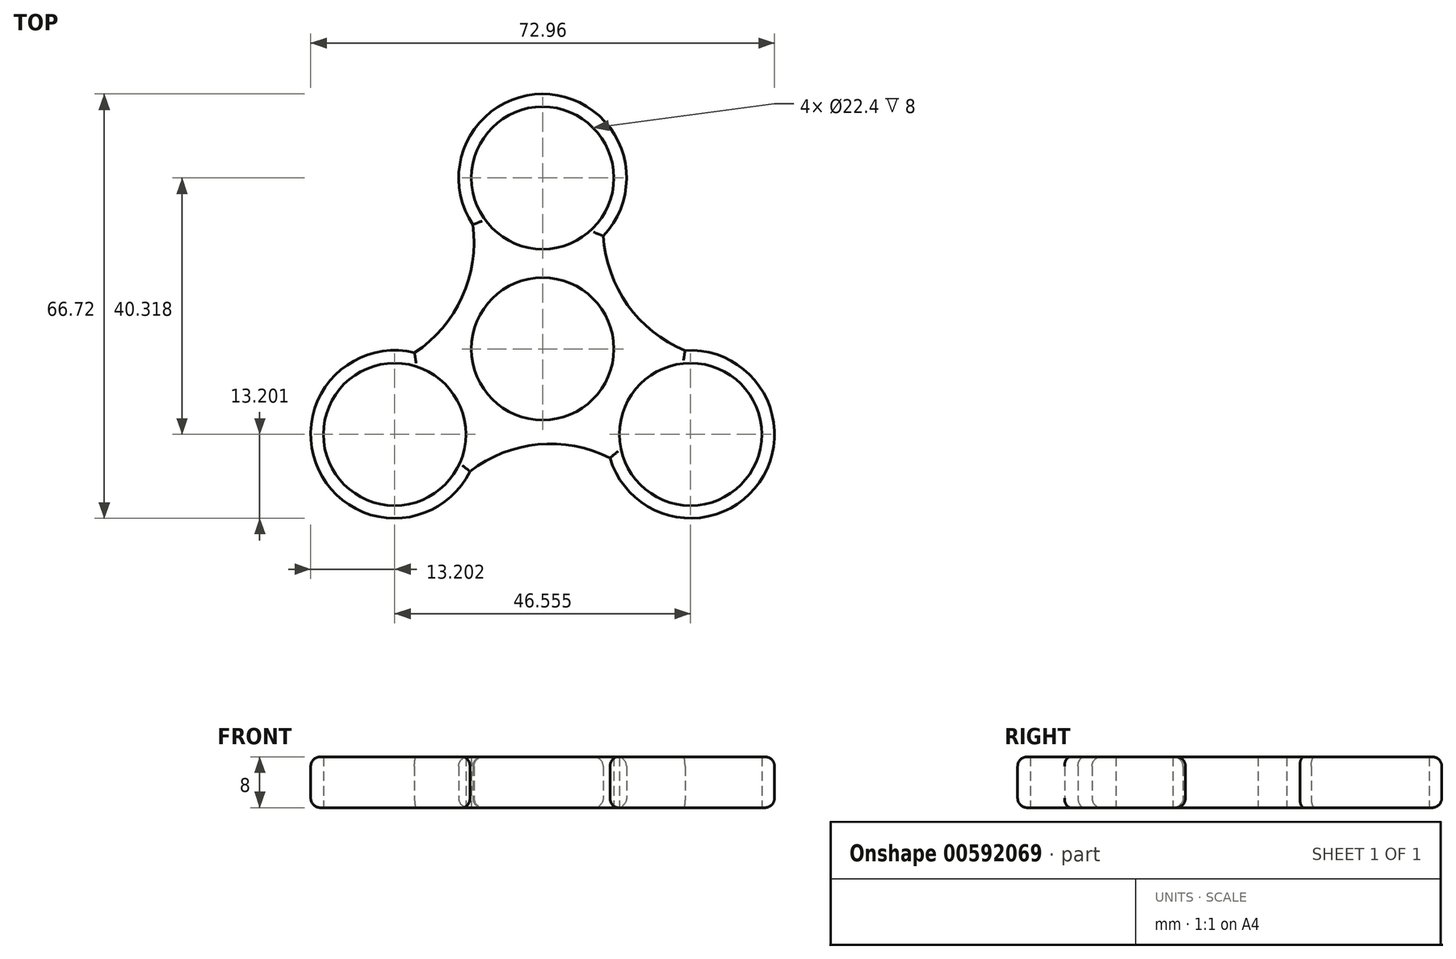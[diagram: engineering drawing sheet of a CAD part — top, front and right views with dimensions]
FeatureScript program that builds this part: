
annotation { "Feature Type Name" : "Feature", "Feature Type Description" : "" }
export const myFeature = defineFeature(function(context is Context, id is Id, definition is map)
    precondition{}
    {
        {
            var Q0;
            Q0=qCreatedBy(makeId("Top.planeOp"),FACE);
            var sketch = newSketch(context, id + "F0", { "sketchPlane" : qUnion([Q0])});
            skCircle(sketch, "E0", {"center": v(0, 0) * mm, "radius": 11.2 * mm});
            skCircle(sketch, "E1", {"center": v(0, 26.88) * mm, "radius": 11.2 * mm});
            skArc(sketch, "E2", {"start": v(9.54, 17.76) * mm, "mid": v(1.14, 40.03) * mm, "end": v(-10.97, 19.54) * mm});
            skArc(sketch, "E3.1.0", {"start": v(-20.15, -0.61) * mm, "mid": v(-35.24, -19.03) * mm, "end": v(-11.43, -19.27) * mm});
            skCircle(sketch, "E3.1.1", {"center": v(-23.28, -13.44) * mm, "radius": 11.2 * mm});
            skArc(sketch, "E3.2.0", {"start": v(10.6, -17.14) * mm, "mid": v(34.1, -21) * mm, "end": v(22.4, -0.27) * mm});
            skCircle(sketch, "E3.2.1", {"center": v(23.28, -13.44) * mm, "radius": 11.2 * mm});
            skArc(sketch, "E4", {"start": v(9.54, 17.76) * mm, "mid": v(13.38, 6.9) * mm, "end": v(22.4, -0.27) * mm});
            skArc(sketch, "E5.1.0", {"start": v(-20.15, -0.61) * mm, "mid": v(-12.66, 8.14) * mm, "end": v(-10.97, 19.54) * mm});
            skArc(sketch, "E5.2.0", {"start": v(10.6, -17.14) * mm, "mid": v(-0.72, -15.04) * mm, "end": v(-11.43, -19.27) * mm});
            skSolve(sketch);
        }
        {
            var Q0;
            Q0=makeQuery(id+"F0.imprint","IMPRINT",FACE,{"disambiguationData":[TD([[makeQuery(id+"F0.imprint","IMPRINT",EDGE,{"derivedFrom":sQuery(id+"F0.wireOp",EDGE,"E0")}),-1.0]])]});
            extrude(context, id + "F1", {"entities" : qUnion([Q0]), "depth" : 8 * mm, "offsetDistance" : 25 * mm});
        }
        {
            var Q0;
            Q0=makeQuery(id+"F1.opExtrude","CAP_EDGE",EDGE,{"disambiguationData":[OSD([sQuery(id+"F0.wireOp",EDGE,"E5.1.0")])],"isStart":false});
            var Q1;
            Q1=makeQuery(id+"F1.opExtrude","CAP_EDGE",EDGE,{"disambiguationData":[OSD([sQuery(id+"F0.wireOp",EDGE,"E3.1.0")])],"isStart":false});
            var Q2;
            Q2=makeQuery(id+"F1.opExtrude","CAP_EDGE",EDGE,{"disambiguationData":[OSD([sQuery(id+"F0.wireOp",EDGE,"E5.2.0")])],"isStart":false});
            var Q3;
            Q3=makeQuery(id+"F1.opExtrude","CAP_EDGE",EDGE,{"disambiguationData":[OSD([sQuery(id+"F0.wireOp",EDGE,"E3.2.0")])],"isStart":false});
            var Q4;
            Q4=makeQuery(id+"F1.opExtrude","CAP_EDGE",EDGE,{"disambiguationData":[OSD([sQuery(id+"F0.wireOp",EDGE,"E4")])],"isStart":false});
            var Q5;
            Q5=makeQuery(id+"F1.opExtrude","CAP_EDGE",EDGE,{"disambiguationData":[OSD([sQuery(id+"F0.wireOp",EDGE,"E2")])],"isStart":false});
            fillet(context, id + "F2", {"entities" : qUnion([Q0, Q1, Q2, Q3, Q4, Q5]), "radius" : 1.5 * mm, "allowEdgeOverflow" : false});
        }
        {
            var Q0;
            Q0=makeQuery(id+"F1.opExtrude","CAP_EDGE",EDGE,{"disambiguationData":[OSD([sQuery(id+"F0.wireOp",EDGE,"E3.1.0")])],"isStart":true});
            var Q1;
            Q1=makeQuery(id+"F1.opExtrude","CAP_EDGE",EDGE,{"disambiguationData":[OSD([sQuery(id+"F0.wireOp",EDGE,"E5.2.0")])],"isStart":true});
            var Q2;
            Q2=makeQuery(id+"F1.opExtrude","CAP_EDGE",EDGE,{"disambiguationData":[OSD([sQuery(id+"F0.wireOp",EDGE,"E3.2.0")])],"isStart":true});
            var Q3;
            Q3=makeQuery(id+"F1.opExtrude","CAP_EDGE",EDGE,{"disambiguationData":[OSD([sQuery(id+"F0.wireOp",EDGE,"E4")])],"isStart":true});
            var Q4;
            Q4=makeQuery(id+"F1.opExtrude","CAP_EDGE",EDGE,{"disambiguationData":[OSD([sQuery(id+"F0.wireOp",EDGE,"E2")])],"isStart":true});
            var Q5;
            Q5=makeQuery(id+"F1.opExtrude","CAP_EDGE",EDGE,{"disambiguationData":[OSD([sQuery(id+"F0.wireOp",EDGE,"E5.1.0")])],"isStart":true});
            fillet(context, id + "F3", {"entities" : qUnion([Q0, Q1, Q2, Q3, Q4, Q5]), "radius" : 1.5 * mm, "tangentPropagation" : true, "allowEdgeOverflow" : false});
        }
    });
